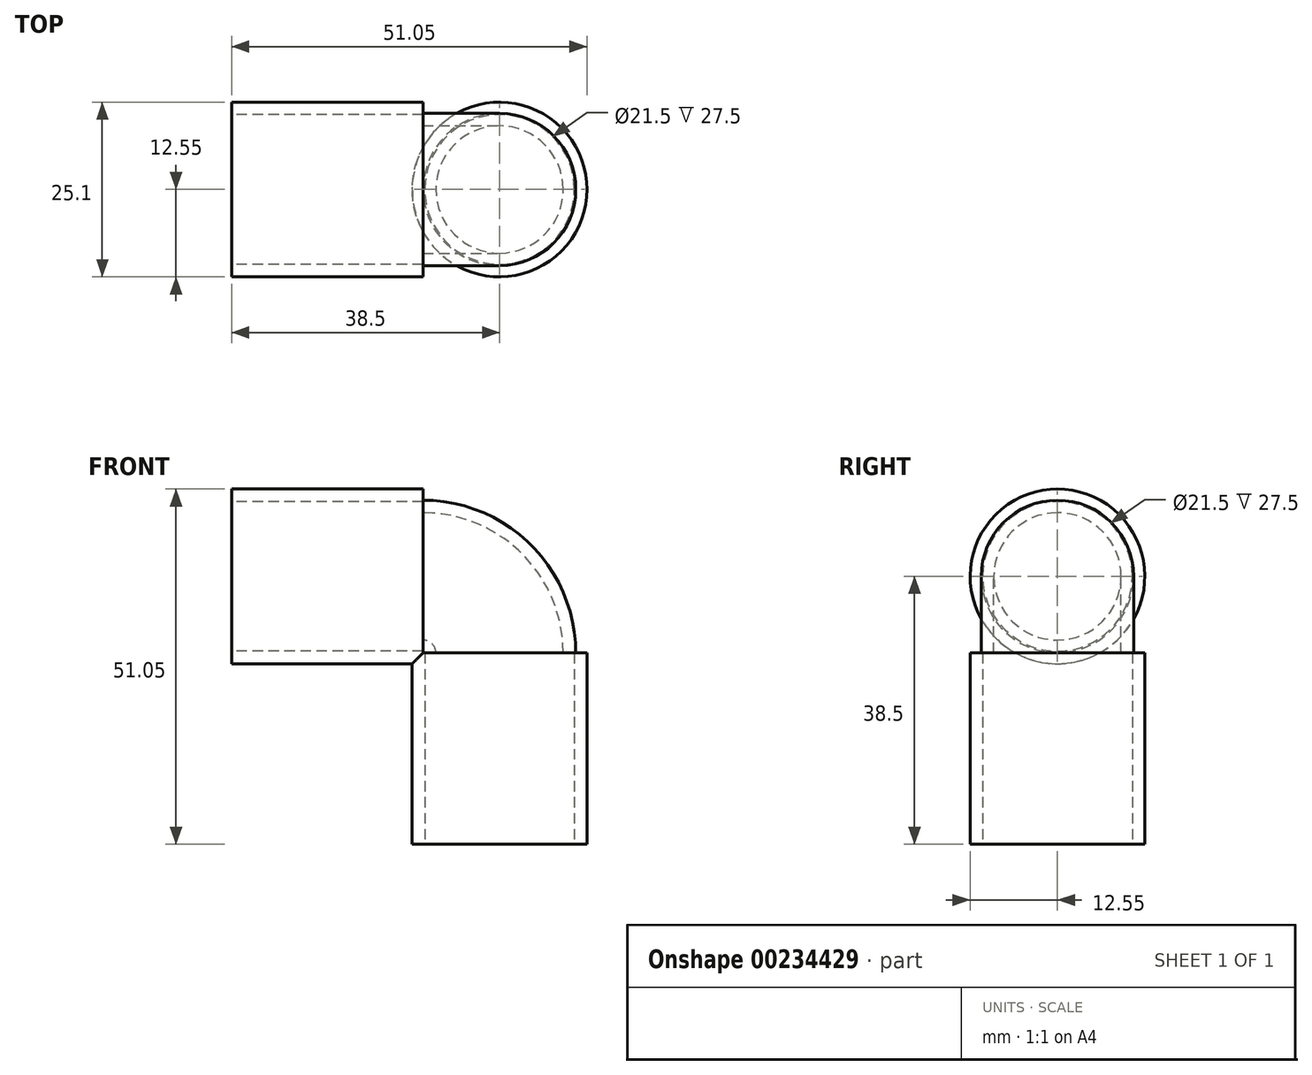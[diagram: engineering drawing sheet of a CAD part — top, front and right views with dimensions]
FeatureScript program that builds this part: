
annotation { "Feature Type Name" : "Feature", "Feature Type Description" : "" }
export const myFeature = defineFeature(function(context is Context, id is Id, definition is map)
    precondition{}
    {
        {
            var Q0;
            Q0=qCreatedBy(makeId("Front.planeOp"),FACE);
            var sketch = newSketch(context, id + "F0", { "sketchPlane" : qUnion([Q0])});
            skArc(sketch, "E0", {"start": v(7.78, 7.78) * mm, "mid": v(10.16, 4.2) * mm, "end": v(11, 0) * mm});
            skLineSegment(sketch, "E1", {"start": v(0, 0) * mm, "end": v(7.78, 7.78) * mm, "construction": true});
            skLineSegment(sketch, "E2.MirrorCS", {"start": v(11, 0) * mm, "end": v(11, -27.5) * mm});
            skPoint(sketch, "E3.orphan", {"position": v(0, 11) * mm});
            skSolve(sketch);
        }
        {
            var Q0;
            Q0=qCreatedBy(makeId("Top.planeOp"),FACE);
            var sketch = newSketch(context, id + "F1", { "sketchPlane" : qUnion([Q0])});
            skPoint(sketch, "E4.0", {"position": v(11, 0) * mm});
            skCircle(sketch, "E5", {"center": v(11, 0) * mm, "radius": 10.95 * mm});
            skCircle(sketch, "E6", {"center": v(11, 0) * mm, "radius": 12.55 * mm});
            skCircle(sketch, "E7", {"center": v(11, 0) * mm, "radius": 10.75 * mm});
            skCircle(sketch, "E8", {"center": v(11, 0) * mm, "radius": 9.15 * mm});
            skSolve(sketch);
        }
        {
            var Q0;
            Q0=makeQuery(id+"F1.imprint","IMPRINT",FACE,{"disambiguationData":[TD([[makeQuery(id+"F1.imprint","IMPRINT",EDGE,{"derivedFrom":sQuery(id+"F1.wireOp",EDGE,"E5")}),1.0]])]});
            var Q1;
            Q1=makeQuery(id+"F1.imprint","IMPRINT",FACE,{"disambiguationData":[TD([[makeQuery(id+"F1.imprint","IMPRINT",EDGE,{"derivedFrom":sQuery(id+"F1.wireOp",EDGE,"E7")}),1.0]])]});
            var Q2;
            Q2=sQuery(id+"F0.wireOp",EDGE,"E0");
            sweep(context, id + "F2", {"profiles" : qUnion([Q0, Q1]), "path" : qUnion([Q2])});
        }
        {
            var Q0;
            Q0=makeQuery(id+"F1.imprint","IMPRINT",FACE,{"disambiguationData":[TD([[makeQuery(id+"F1.imprint","IMPRINT",EDGE,{"derivedFrom":sQuery(id+"F1.wireOp",EDGE,"E5")}),1.0]])]});
            var Q1;
            Q1=makeQuery(id+"F1.imprint","IMPRINT",FACE,{"disambiguationData":[TD([[makeQuery(id+"F1.imprint","IMPRINT",EDGE,{"derivedFrom":sQuery(id+"F1.wireOp",EDGE,"E5")}),-1.0]])]});
            var Q2;
            Q2=sQuery(id+"F0.wireOp",EDGE,"E2.MirrorCS");
            sweep(context, id + "F3", {"operationType" : NewBodyOperationType.ADD, "profiles" : qUnion([Q0, Q1]), "path" : qUnion([Q2])});
        }
        {
            var Q0;
            Q0=makeQuery(id+"F2.opSweep","SWEPT_BODY",BODY,{"disambiguationData":[OSD([sQuery(id+"F0.wireOp",EDGE,"E0"),sQuery(id+"F1.wireOp",EDGE,"E5"),sQuery(id+"F1.wireOp",EDGE,"E8")])]});
            var Q1;
            Q1=makeQuery(id+"F2.opSweep","CAP_FACE",FACE,{"disambiguationData":[OSD([sQuery(id+"F0.wireOp",VERTEX,"E0.start"),sQuery(id+"F1.wireOp",EDGE,"E5"),sQuery(id+"F1.wireOp",EDGE,"E8")])],"isStart":false});
            mirror(context, id + "F4", {"operationType" : NewBodyOperationType.ADD, "entities" : qUnion([Q0]), "mirrorPlane" : qUnion([Q1])});
        }
    });
